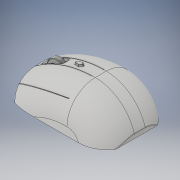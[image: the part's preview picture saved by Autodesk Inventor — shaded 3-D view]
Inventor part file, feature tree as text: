
AUTODESK INVENTOR PART (.ipt)
format: ipt  version: 2017 (Build 210142000, 142)  size: 1,084,416 bytes
history: native  units: in
note: dims shown in document units (in); Inventor stores cm internally (conversion verified against a paired STEP export)
features: sketch x12, other x8, extrude x7, fillet x5, sweep x2, mirror x1
ambient origin geometry x8: Origin, YZ Plane, XZ Plane, XY Plane, X Axis, Y Axis, Z Axis, Center Point
bodies: Solid1 (feature_tree)
feature tree (35):
  extrude  "main body"  Depth=0.1251in
  other  "middle of the mouse workplane"
  fillet  "curve the edges"  Radius=0.0409in
  other  "gap for mouse clicks"
  sweep  "gap made for mouse clicks"
  sweep  "gap for mouse clicks front"
  extrude  "far left gap for mouse clicks"  Depth=0.2314in TaperAngle=0.0deg
  mirror  "mirror mouse clicks for other side"
  extrude  "mouse wheel gap"  Depth=0.1974in
  extrude  "mouse wheel extion for proper width"  Depth=0.0053in
  fillet  "curve proper width for wheel gap"  [1 undecoded]
  other  "mouse wheel revolve plane"
  other  "wheel"
  extrude  "friction points"  Depth=0.0302in
  fillet  "wheel curve edge"  Radius=0.0046in
  other  "batter indicator workplane"
  extrude  "battery indicator cut out"  Depth=0.0199in TaperAngle=0.0deg
  extrude  "power indicator"  Depth=0.0687in
  fillet  "smooth the power indicator"  Radius=0.0382in
  fillet  "smooth front and back edges"  Radius=0.0043in
  other  "used to find the middle front to back"
  other  "middle of the mouse front to back"
  sketch  "Sketch1"  dims[d0=0.3403in d1=0.1251in d2=0.0409in]
  sketch  "Sketch3"  dims[d3=0.014in d4=0.3157in]
  sketch  "Sketch4"  dims[d5=0.0247in d6=0.1333in]
  sketch  "Sketch6"  dims[d7=0.0143in d8=0.2314in d9=0.0in]
  sketch  "Sketch8"  dims[d10=0.097in d13=0.1974in]
  sketch  "Sketch10"  dims[d14=0.0018in d15=0.0053in d16=0.0in d17=0.0in]
  sketch  "Sketch11"  dims[d18=0.0167in d19=0.0302in d20=0.0046in]
  other  "Work Axis1"
  sketch  "Sketch12"  dims[d21=0.0046in d24=0.0199in d25=0.0in]
  sketch  "Sketch13"  dims[d26=0.003in d28=0.0687in d29=0.0382in d30=0.0043in]
  sketch  "Sketch16"  dims[d31=105.0deg]
  sketch  "3D Sketch2"
  sketch  "Sketch18"  dims[d32=105.0deg d33=0.0203in d34=0.0146in d35=0.0199in d36=0.0in d37=0.0636in d38=0.0156in d39=0.0156in d40=0.003in d41=0.0734in d45=0.0169in d46=0.0299in d47=0.0in d48=0.005in d50=0.0019in d51=90.0deg d52=0.0081in d53=0.001in d54=0.0318in d56=90.0deg d62=41.3386in d64=360.0deg d66=0.0163in d67=0.0143in d68=0.0in d69=0.001in d89=105.0deg d90=105.0deg d91=0.002in d93=0.002in d94=0.002in d97=0.0101in d98=0.0in d99=0.001in d103=0.0053in d104=0.0018in d110=0.0583in d113=0.0in d114=0.0in d116=0.1974in d117=0.1974in d118=0.0018in d119=0.0in d120=0.0018in d121=0.005in d122=90.0deg]
note: 1 required parameter value undecoded (feature->parameter linkage not recoverable at this tier; creation-order binding heuristic only, values carry confidence <= 0.55)
